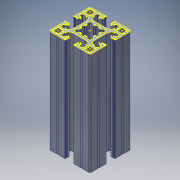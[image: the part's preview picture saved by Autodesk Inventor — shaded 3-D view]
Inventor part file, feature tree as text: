
AUTODESK INVENTOR PART (.ipt)
format: ipt  version: 2018 (Build 220112000, 112)  size: 685,056 bytes
history: native  units: mm
features: other x3, sketch x1
ambient origin geometry x8: Origin, YZ Plane, XZ Plane, XY Plane, X Axis, Y Axis, Z Axis, Center Point
bodies: Body1 (feature_tree)
feature tree (4):
  other  "Sólido1"
  sketch  "Esboço1"
  other  "Contorno projetado1"
  other  "Quadrado PF40-01 - PERFIL 4040 BÁSICO(1)"
